# Revit family: RN 86500 Optiflex-Flowpress-Valvola diritta
name_source: partatom
category: Rohrzubehör
units: mm (PartAtom-declared; Revit-internal decimal feet)

## family parameters
Arbeitsebenenbasiert = Nein
Beim Laden mit Abzugskörper schneiden = Nein
Bemaßung runder Anschluss = Durchmesser verwenden
Gemeinsam genutzt = Nein
Immer vertikal = Ja
Teiletyp = Ventil - Zerlegung in

## types (3) — shared parameters
1.010.00.2 Blattnummer der Richtlinie = 17
1.010.00.3 Ausgabedatum (Monat) der Richtlinie = 201601
1.010.00.4 Herstellername = R. Nussbaum AG
1.010.00.5 Revisionsdatum der Datei = 20190528
1.010.00.6 Webadresse des Herstellers = http://www.nussbaum.ch
1.100.00.3 Sortiernummer für Anzeigereihenfolge = 1
1.100.00.4 Produktbezeichnung = Absperrarmaturen
1.960/3L.00.8 Link (URL) = https://www.nussbaum.ch
17.700.00.4 Armaturentyp = 1
17.700.00.7 Maximale Betriebstemperatur TB [°C] = 70
17.700.00.8 Maximaler Betriebsdruck (Arbeitsdruck) ps [1.0 · 105 Pa] = 10
Connector Visibility = Nein
EnclosingSpace Visibility = Nein
Hersteller = R. Nussbaum AG
URL = https://www.nussbaum.ch

## per-type parameters (varying)
| type | 1.800.00.3 TGA-Nummer | 1.810.00.3 Hersteller-Bestellnummer | 1.810.00.4 DATANORM-Nummer | 1.810.00.5 StLB-Nummer | 1.810.00.6 GTIN-Nummer | 17.700.00.30 Produktbeschreibung | 17.700.00.5 Nennweite DN | 17.700.00.6 kvs-Wert [m3/h] | CONNECTOR0_DIAMETER_dX_0r | CONNECTOR0_dX_00 | CONNECTOR0_dX_01 | CONNECTOR0_ref_dX | CONNECTOR1_DIAMETER_dX_0r | CONNECTOR1_dX_00 | CONNECTOR1_dX_01 | CONNECTOR1_ref_dX | Modell | R. Nussbaum AG 86500.24 de Visibility | R. Nussbaum AG 86500.25 de Visibility | R. Nussbaum AG 86500.26 de Visibility | Typenkommentare |
| DN 20 | 001054???00000000000000000000200700000000000000001???00000 | 86500.24 | 86500.24 | 381.463 | 7612945730473 | 86500.24, Optiflex-Flowpress-Geradsitzventil, Ausgang mit Aussengewinde, DN=20, R | 20 | 5.6 | 20 mm | 50 mm | 36 mm | 36 mm | 20 mm | 36 mm | 51 mm | 36 mm | 86500.24 | Ja | Nein | Nein | Optiflex-Flowpress-Geradsitzventil DN 20 |
| DN 25 | 001054???0000000000000000000020070000000000000000200000000 | 86500.25 | 86500.25 | 381.464 | 7612945730480 | 86500.25, Optiflex-Flowpress-Geradsitzventil, Ausgang mit Aussengewinde, DN=25, R | 25 | 9.3 | 25 mm  [stored 0.082021 ft] | 59 mm | 39 mm | 39 mm | 25 mm  [stored 0.082021 ft] | 40 mm | 57 mm | 40 mm | 86500.25 | Nein | Ja | Nein | Optiflex-Flowpress-Geradsitzventil DN 25 |
| DN 32 | 001054???0000000000000000000020070000000000000000300000000 | 86500.26 | 86500.26 |  | 7612945730497 | 86500.26, Optiflex-Flowpress-Geradsitzventil, Ausgang mit Aussengewinde, DN=32, R | 32 | 15.4 | 32 mm | 70 mm | 44 mm | 44 mm | 32 mm | 47 mm | 66 mm | 47 mm | 86500.26 | Nein | Nein | Ja | Optiflex-Flowpress-Geradsitzventil DN 32 |

note: [stored X ft] marks values corroborated as IEEE doubles in the binary element streams (Revit-internal decimal feet)

## geometry (parser evidence)
native form markers: Sweep x1
no freeform markers — native parametric forms only
